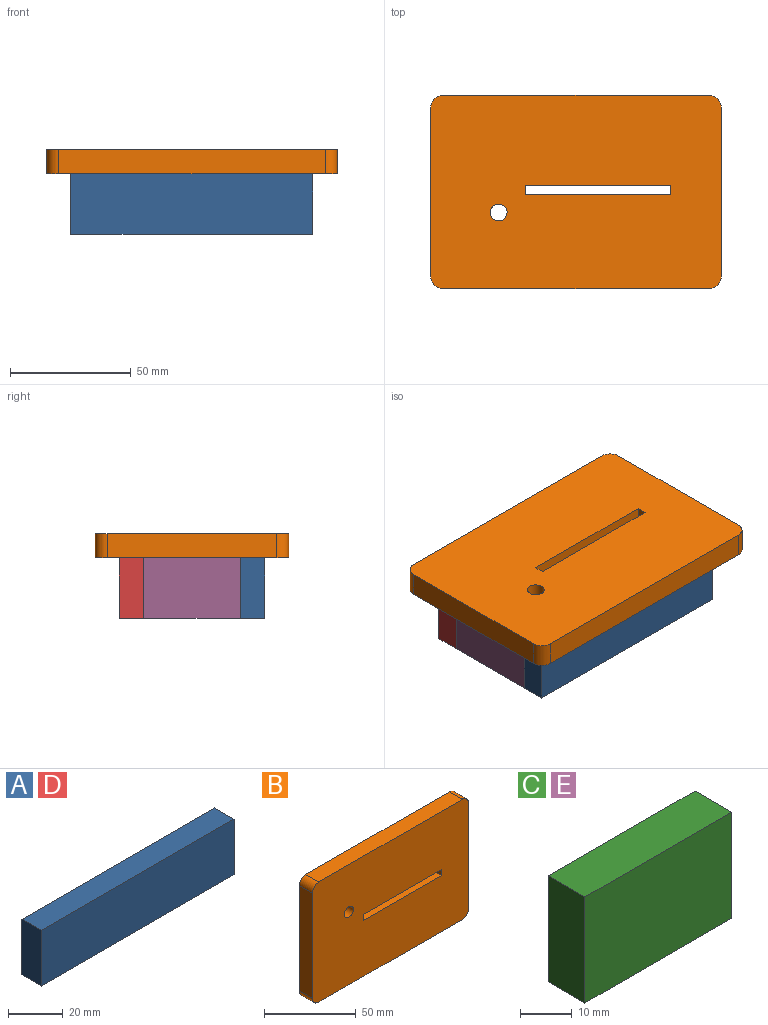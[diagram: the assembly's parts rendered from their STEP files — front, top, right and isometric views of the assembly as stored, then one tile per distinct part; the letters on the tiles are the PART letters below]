
ASSEMBLY  parts=5 mates=4
PART A: 6 faces, bbox 100x10x25 mm
  f0: plane 25x10mm, normal (1,0,0), area 250mm2, adj f1,f3,f4,f5
  f1: plane 100x10mm, normal (0,0,1), area 1000mm2, adj f0,f2,f4,f5
  f2: plane 25x10mm, normal (-1,0,0), area 250mm2, adj f1,f3,f4,f5
  f3: plane 100x10mm, normal (0,0,-1), area 1000mm2, adj f0,f2,f4,f5
  f4: plane 100x25mm, normal (0,-1,0), area 2500mm2, adj f0,f1,f2,f3
  f5: plane 100x25mm, normal (0,1,0), area 2500mm2, adj f0,f1,f2,f3
PART B: 15 faces, bbox 120x10x80 mm
  f0: plane 120x80mm, normal (0,-1,0), area 9300.1mm2, adj f2,f3,f4,f5,f6,f7,f8,f9
  f1: plane 120x80mm, normal (0,1,0), area 9300.1mm2, adj f2,f3,f4,f5,f6,f7,f8,f9
  f2: plane 70x10mm, normal (1,0,0), area 700mm2, adj f0,f1,f6,f9
  f3: plane 110x10mm, normal (0,0,1), area 1100mm2, adj f0,f1,f6,f7
  f4: plane 70x10mm, normal (-1,0,0), area 700mm2, adj f0,f1,f7,f8
  f5: plane 110x10mm, normal (0,0,-1), area 1100mm2, adj f0,f1,f8,f9
  f6: cylinder r=5mm len=10mm, axis (0,-1,0), area 78.5mm2, adj f0,f1,f2,f3
  f7: cylinder r=5mm len=10mm, axis (0,1,0), area 78.5mm2, adj f0,f1,f3,f4
  f8: cylinder r=5mm len=10mm, axis (0,-1,0), area 78.5mm2, adj f0,f1,f4,f5
  f9: cylinder r=5mm len=10mm, axis (0,1,0), area 78.5mm2, adj f0,f1,f2,f5
  f10: plane 10x4mm, normal (-1,0,0), area 40mm2, adj f0,f1,f11,f13
  f11: plane 60x10mm, normal (0,0,-1), area 600mm2, adj f0,f1,f10,f12
  f12: plane 10x4mm, normal (1,0,0), area 40mm2, adj f0,f1,f11,f13
  f13: plane 60x10mm, normal (0,0,1), area 600mm2, adj f0,f1,f10,f12
  f14: cylinder r=3.5mm len=10mm, axis (0,-1,0), area 219.9mm2, adj f0,f1
PART C: 6 faces, bbox 40x10x25 mm
  f0: plane 25x10mm, normal (1,0,0), area 250mm2, adj f1,f3,f4,f5
  f1: plane 40x10mm, normal (0,0,1), area 400mm2, adj f0,f2,f4,f5
  f2: plane 25x10mm, normal (-1,0,0), area 250mm2, adj f1,f3,f4,f5
  f3: plane 40x10mm, normal (0,0,-1), area 400mm2, adj f0,f2,f4,f5
  f4: plane 40x25mm, normal (0,-1,0), area 1000mm2, adj f0,f1,f2,f3
  f5: plane 40x25mm, normal (0,1,0), area 1000mm2, adj f0,f1,f2,f3
PART D: same geometry as A
PART E: same geometry as C
PLACE A t=(-25.11,-36.56,-32.39)mm fixed
PLACE B rot(axis=(1,0,0),90deg) t=(-96.14,22.22,-3.85)mm
PLACE C rot(axis=(0.71,0.71,0),180deg) t=(8.44,-39.29,-11.61)mm
PLACE D t=(-25.11,13.44,-32.39)mm
PLACE E rot(axis=(0,0,-1),90deg) t=(-81.56,6.17,-41.1)mm
MATE fastened B.f0 <-> D.f1  axis (0,0,-1) through (-41.56,-16.56,-13.85)mm
MATE fastened C.f0 <-> D.f4  axis (0,1,0) through (3.44,3.44,-26.35)mm
MATE fastened E.f2 <-> D.f4  axis (0,1,0) through (-86.56,3.44,-26.35)mm
MATE fastened C.f2 <-> A.f5  axis (0,-1,0) through (3.44,-36.56,-26.35)mm
